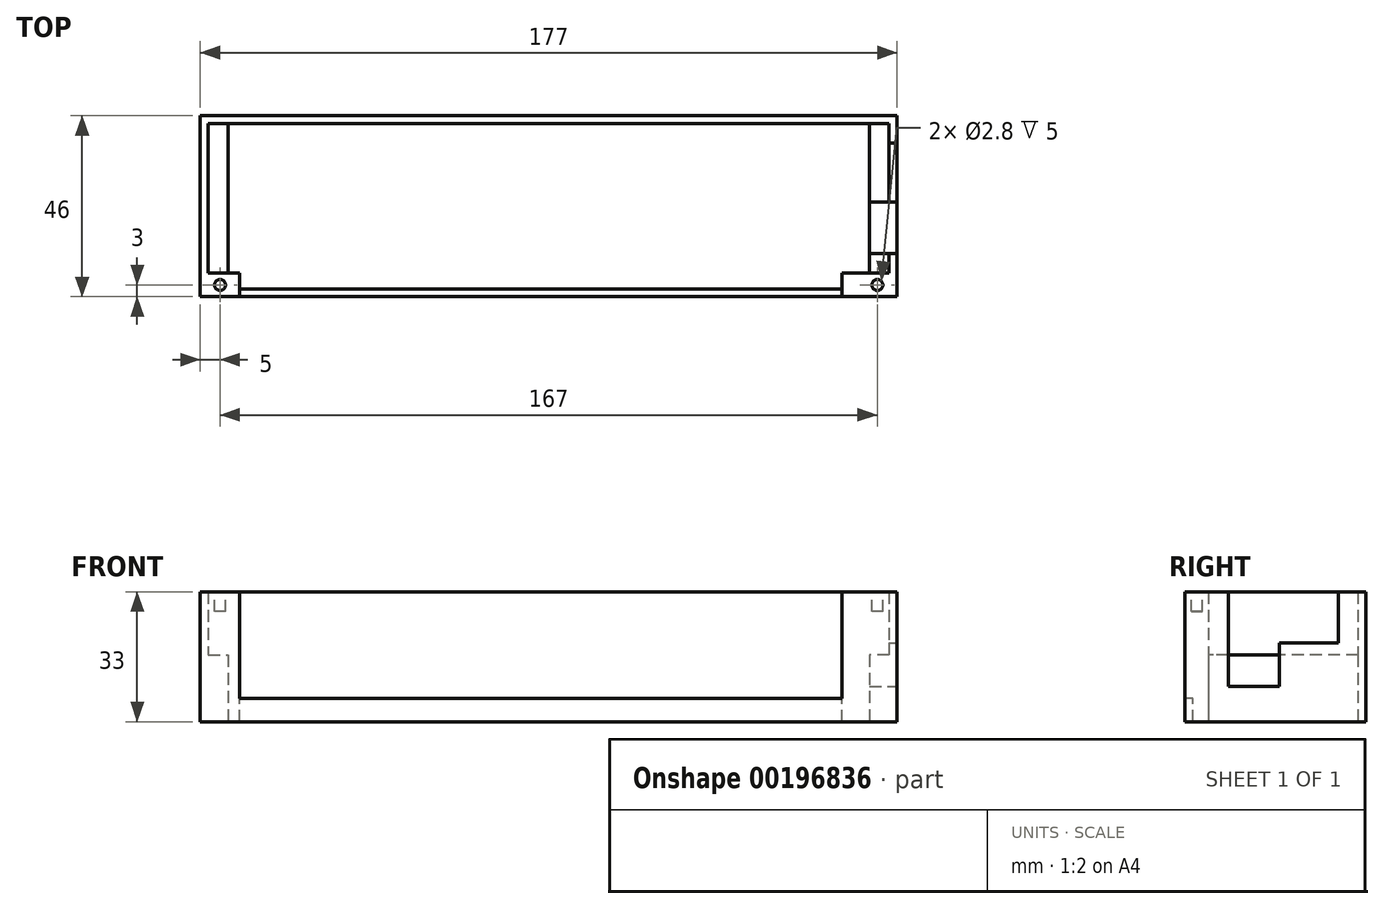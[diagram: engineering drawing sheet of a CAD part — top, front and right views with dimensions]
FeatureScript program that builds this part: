
annotation { "Feature Type Name" : "Feature", "Feature Type Description" : "" }
export const myFeature = defineFeature(function(context is Context, id is Id, definition is map)
    precondition{}
    {
        {
            var Q0;
            Q0=qCreatedBy(makeId("Top.planeOp"),FACE);
            var sketch = newSketch(context, id + "F0", { "sketchPlane" : qUnion([Q0])});
            skLineSegment(sketch, "E0.bottom", {"start": v(88.5, -23) * mm, "end": v(-88.5, -23) * mm});
            skLineSegment(sketch, "E0.top", {"start": v(88.5, 23) * mm, "end": v(-88.5, 23) * mm});
            skLineSegment(sketch, "E0.left", {"start": v(88.5, -23) * mm, "end": v(88.5, 23) * mm});
            skLineSegment(sketch, "E0.right", {"start": v(-88.5, -23) * mm, "end": v(-88.5, 23) * mm});
            skPoint(sketch, "E0.middle", {"position": v(0, 0) * mm});
            skLineSegment(sketch, "E1.bottom", {"start": v(-86.5, 21) * mm, "end": v(86.5, 21) * mm});
            skLineSegment(sketch, "E1.top", {"start": v(-86.5, -17) * mm, "end": v(86.5, -17) * mm});
            skLineSegment(sketch, "E1.left", {"start": v(-86.5, 21) * mm, "end": v(-86.5, -17) * mm});
            skLineSegment(sketch, "E1.right", {"start": v(86.5, 21) * mm, "end": v(86.5, -17) * mm});
            skSolve(sketch);
        }
        {
            var Q0;
            Q0 = qSketchRegion(id + "F0", true);
            extrude(context, id + "F1", {"entities" : qUnion([Q0]), "depth" : 33 * mm});
        }
        {
            var Q0;
            Q0=makeQuery(id+"F1.opExtrude","SWEPT_FACE",FACE,{"disambiguationData":[OSD([sQuery(id+"F0.wireOp",EDGE,"E0.bottom")])]});
            var sketch = newSketch(context, id + "F2", { "sketchPlane" : qUnion([Q0])});
            skLineSegment(sketch, "E2.bottom", {"start": v(-78.5, 33) * mm, "end": v(74.5, 33) * mm});
            skLineSegment(sketch, "E2.top", {"start": v(-78.5, 6) * mm, "end": v(74.5, 6) * mm});
            skLineSegment(sketch, "E2.left", {"start": v(-78.5, 33) * mm, "end": v(-78.5, 6) * mm});
            skLineSegment(sketch, "E2.right", {"start": v(74.5, 33) * mm, "end": v(74.5, 6) * mm});
            skSolve(sketch);
        }
        {
            var Q0;
            Q0 = qSketchRegion(id + "F2", true);
            extrude(context, id + "F3", {"entities" : qUnion([Q0]), "operationType" : NewBodyOperationType.REMOVE, "oppositeDirection" : true, "depth" : 6 * mm});
        }
        {
            var Q0;
            Q0=qCreatedBy(makeId("Top.planeOp"),FACE);
            var sketch = newSketch(context, id + "F4", { "sketchPlane" : qUnion([Q0])});
            skLineSegment(sketch, "E3.bottom", {"start": v(-86.5, 21) * mm, "end": v(-81.5, 21) * mm});
            skLineSegment(sketch, "E3.top", {"start": v(-86.5, -17) * mm, "end": v(-81.5, -17) * mm});
            skLineSegment(sketch, "E3.left", {"start": v(-86.5, 21) * mm, "end": v(-86.5, -17) * mm});
            skLineSegment(sketch, "E3.right", {"start": v(-81.5, 21) * mm, "end": v(-81.5, -17) * mm});
            skLineSegment(sketch, "E4.bottom", {"start": v(86.5, 21) * mm, "end": v(81.5, 21) * mm});
            skLineSegment(sketch, "E4.top", {"start": v(86.5, -17) * mm, "end": v(81.5, -17) * mm});
            skLineSegment(sketch, "E4.left", {"start": v(86.5, 21) * mm, "end": v(86.5, -17) * mm});
            skLineSegment(sketch, "E4.right", {"start": v(81.5, 21) * mm, "end": v(81.5, -17) * mm});
            skSolve(sketch);
        }
        {
            var Q0;
            Q0 = qSketchRegion(id + "F4", true);
            extrude(context, id + "F5", {"entities" : qUnion([Q0]), "operationType" : NewBodyOperationType.ADD, "depth" : 17 * mm});
        }
        {
            var Q0;
            Q0=makeQuery(id+"F1.opExtrude","SWEPT_FACE",FACE,{"disambiguationData":[OSD([sQuery(id+"F0.wireOp",EDGE,"E0.left")])]});
            var sketch = newSketch(context, id + "F6", { "sketchPlane" : qUnion([Q0])});
            skLineSegment(sketch, "E5.bottom", {"start": v(-12, 33) * mm, "end": v(16, 33) * mm});
            skLineSegment(sketch, "E5.top", {"start": v(-12, 20) * mm, "end": v(16, 20) * mm});
            skLineSegment(sketch, "E5.left", {"start": v(-12, 33) * mm, "end": v(-12, 20) * mm});
            skLineSegment(sketch, "E5.right", {"start": v(16, 33) * mm, "end": v(16, 20) * mm});
            skLineSegment(sketch, "E6.bottom", {"start": v(-12, 20) * mm, "end": v(1, 20) * mm});
            skLineSegment(sketch, "E6.top", {"start": v(-12, 9) * mm, "end": v(1, 9) * mm});
            skLineSegment(sketch, "E6.left", {"start": v(-12, 20) * mm, "end": v(-12, 9) * mm});
            skLineSegment(sketch, "E6.right", {"start": v(1, 20) * mm, "end": v(1, 9) * mm});
            skSolve(sketch);
        }
        {
            var Q0;
            Q0 = qSketchRegion(id + "F6", true);
            extrude(context, id + "F7", {"entities" : qUnion([Q0]), "operationType" : NewBodyOperationType.REMOVE, "oppositeDirection" : true, "depth" : 25 * mm});
        }
        {
            var Q0;
            Q0=qCreatedBy(makeId("Top.planeOp"),FACE);
            cPlane(context, id + "F8", {"entities" : qUnion([Q0]), "cplaneType" : CPlaneType.OFFSET, "offset" : 33 * mm, "width" : 150 * mm, "height" : 150 * mm});
        }
        {
            var Q0;
            Q0=qCreatedBy(id+"F8.planeOp",FACE);
            var sketch = newSketch(context, id + "F9", { "sketchPlane" : qUnion([Q0])});
            skCircle(sketch, "E7", {"center": v(-83.5, -20) * mm, "radius": 1.4 * mm});
            skCircle(sketch, "E8", {"center": v(83.5, -20) * mm, "radius": 1.4 * mm});
            skSolve(sketch);
        }
        {
            var Q0;
            Q0 = qSketchRegion(id + "F9", true);
            extrude(context, id + "F10", {"entities" : qUnion([Q0]), "operationType" : NewBodyOperationType.REMOVE, "oppositeDirection" : true, "depth" : 5 * mm});
        }
        {
            var Q0;
            Q0=makeQuery(id+"F3.boolean.opBoolean","COPY",FACE,{"derivedFrom":makeQuery(id+"F3.opExtrude","SWEPT_FACE",FACE,{"disambiguationData":[OSD([sQuery(id+"F2.wireOp",EDGE,"E2.top")])]})});
            var sketch = newSketch(context, id + "F11", { "sketchPlane" : qUnion([Q0])});
            skLineSegment(sketch, "E9.bottom", {"start": v(-78.5, -17) * mm, "end": v(74.5, -17) * mm});
            skLineSegment(sketch, "E9.top", {"start": v(-78.5, -21) * mm, "end": v(74.5, -21) * mm});
            skLineSegment(sketch, "E9.left", {"start": v(-78.5, -17) * mm, "end": v(-78.5, -21) * mm});
            skLineSegment(sketch, "E9.right", {"start": v(74.5, -17) * mm, "end": v(74.5, -21) * mm});
            skSolve(sketch);
        }
        {
            var Q0;
            Q0 = qSketchRegion(id + "F11", true);
            extrude(context, id + "F12", {"entities" : qUnion([Q0]), "operationType" : NewBodyOperationType.REMOVE, "oppositeDirection" : true, "depth" : 6 * mm});
        }
    });
